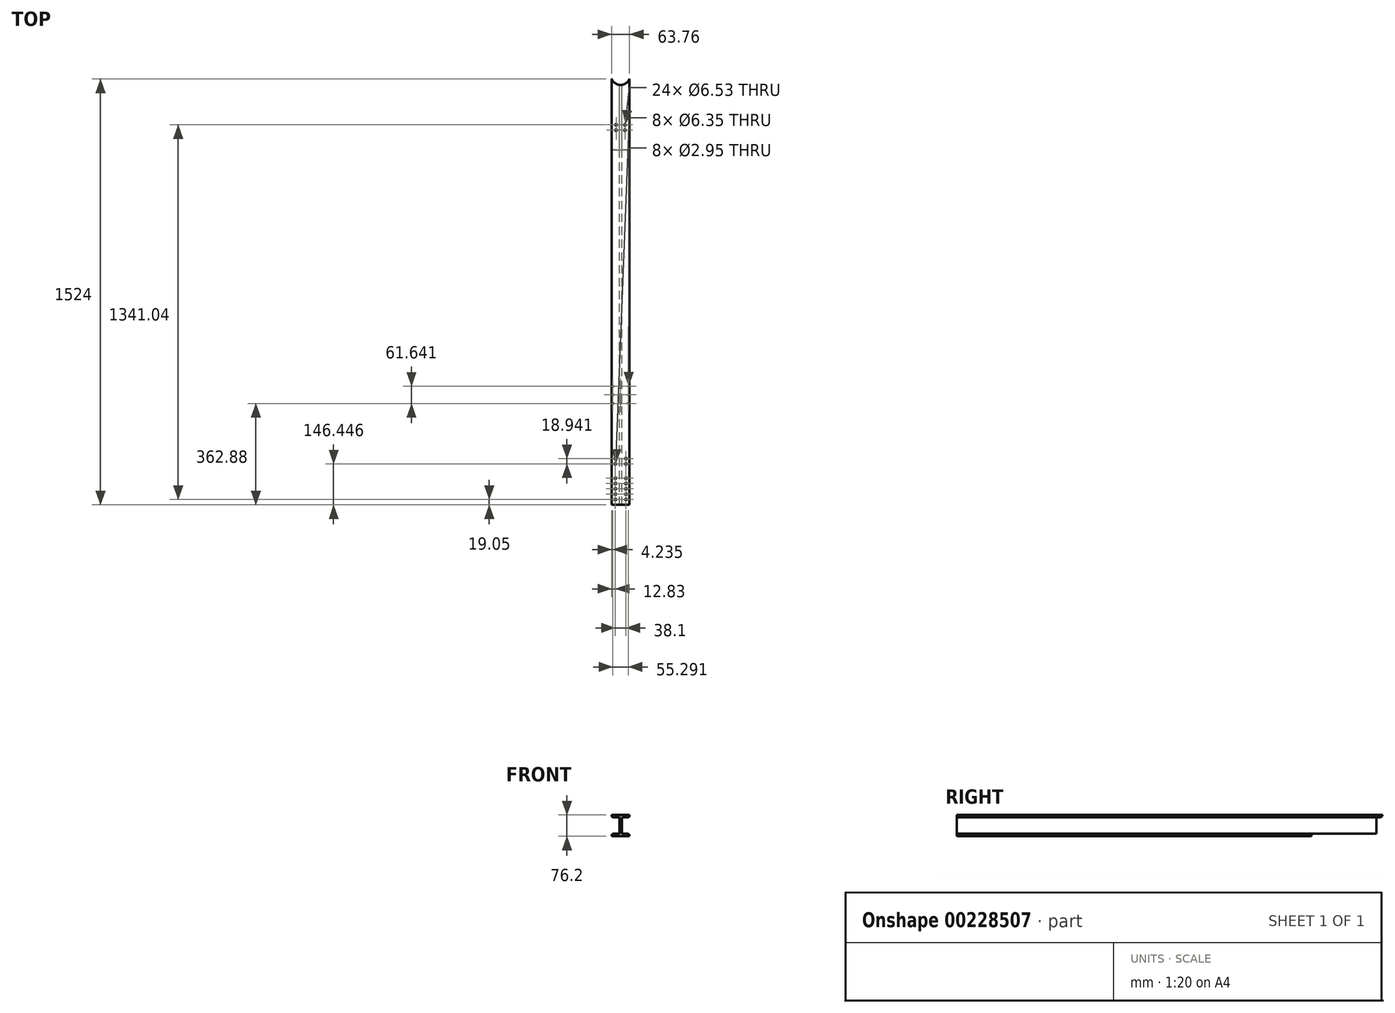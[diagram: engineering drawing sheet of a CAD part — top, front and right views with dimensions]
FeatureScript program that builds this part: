
annotation { "Feature Type Name" : "Feature", "Feature Type Description" : "" }
export const myFeature = defineFeature(function(context is Context, id is Id, definition is map)
    precondition{}
    {
        {
            var Q0;
            Q0=qCreatedBy(makeId("Front.planeOp"),FACE);
            var sketch = newSketch(context, id + "F0", { "sketchPlane" : qUnion([Q0])});
            skLineSegment(sketch, "E0", {"start": v(0, 0) * mm, "end": v(0, 38.1) * mm});
            skLineSegment(sketch, "E1", {"start": v(0, 38.1) * mm, "end": v(31.88, 38.1) * mm});
            skLineSegment(sketch, "E2", {"start": v(31.88, 38.1) * mm, "end": v(31.88, 35.56) * mm});
            skLineSegment(sketch, "E3", {"start": v(0, 0) * mm, "end": v(4.45, 0) * mm});
            skLineSegment(sketch, "E4", {"start": v(4.45, 0) * mm, "end": v(4.45, 29.2) * mm});
            skLineSegment(sketch, "E5", {"start": v(4.44, 29.2) * mm, "end": v(25.53, 29.2) * mm});
            skPoint(sketch, "E6.visualSharp", {"position": v(31.88, 29.2) * mm});
            skArc(sketch, "E6.filletArc", {"start": v(25.53, 29.2) * mm, "mid": v(30.02, 31.07) * mm, "end": v(31.88, 35.56) * mm});
            skLineSegment(sketch, "E7.MirrorCS", {"start": v(4.45, 0) * mm, "end": v(4.45, -29.2) * mm});
            skLineSegment(sketch, "E8.MirrorCS", {"start": v(4.44, -29.2) * mm, "end": v(25.53, -29.2) * mm});
            skLineSegment(sketch, "E9.MirrorCS", {"start": v(0, 0) * mm, "end": v(0, -38.1) * mm});
            skLineSegment(sketch, "E10.MirrorCS", {"start": v(0, -38.1) * mm, "end": v(31.88, -38.1) * mm});
            skArc(sketch, "E11.MirrorCS", {"start": v(25.53, -29.2) * mm, "mid": v(30.02, -31.07) * mm, "end": v(31.88, -35.56) * mm});
            skLineSegment(sketch, "E12.MirrorCS", {"start": v(31.88, -38.1) * mm, "end": v(31.88, -35.56) * mm});
            skLineSegment(sketch, "E13.MirrorCS", {"start": v(0, 38.1) * mm, "end": v(-31.88, 38.1) * mm});
            skLineSegment(sketch, "E14.MirrorCS", {"start": v(-31.88, 38.1) * mm, "end": v(-31.88, 35.56) * mm});
            skArc(sketch, "E15.MirrorCS", {"start": v(-25.53, 29.2) * mm, "mid": v(-30.02, 31.07) * mm, "end": v(-31.88, 35.56) * mm});
            skLineSegment(sketch, "E16.MirrorCS", {"start": v(-4.44, 29.2) * mm, "end": v(-25.53, 29.2) * mm});
            skLineSegment(sketch, "E17.MirrorCS", {"start": v(-4.45, 0) * mm, "end": v(-4.45, -29.2) * mm});
            skLineSegment(sketch, "E18.MirrorCS", {"start": v(-4.44, -29.2) * mm, "end": v(-25.53, -29.2) * mm});
            skArc(sketch, "E19.MirrorCS", {"start": v(-25.53, -29.2) * mm, "mid": v(-30.02, -31.07) * mm, "end": v(-31.88, -35.56) * mm});
            skLineSegment(sketch, "E20.MirrorCS", {"start": v(-4.45, 0) * mm, "end": v(-4.45, 29.2) * mm});
            skLineSegment(sketch, "E21.MirrorCS", {"start": v(-31.88, -38.1) * mm, "end": v(-31.88, -35.56) * mm});
            skLineSegment(sketch, "E22.MirrorCS", {"start": v(0, -38.1) * mm, "end": v(-31.88, -38.1) * mm});
            skSolve(sketch);
        }
        {
            var Q0;
            Q0 = qSketchRegion(id + "F0", true);
            extrude(context, id + "F1", {"entities" : qUnion([Q0]), "depth" : 1524 * mm});
        }
        {
            var Q0;
            Q0=makeQuery(id+"F1.opExtrude","SWEPT_FACE",FACE,{"disambiguationData":[OSD([sQuery(id+"F0.wireOp",EDGE,"E1"),sQuery(id+"F0.wireOp",EDGE,"E13.MirrorCS")])]});
            var sketch = newSketch(context, id + "F2", { "sketchPlane" : qUnion([Q0])});
            skLineSegment(sketch, "E23", {"start": v(0, -35.6) * mm, "end": v(0, 13.64) * mm});
            skCircle(sketch, "E24", {"center": v(0, 13.64) * mm, "radius": 34.67 * mm});
            skLineSegment(sketch, "E25", {"start": v(0, 0) * mm, "end": v(-31.88, 0) * mm});
            skSolve(sketch);
        }
        {
            var Q0;
            Q0 = qSketchRegion(id + "F2", true);
            extrude(context, id + "F3", {"entities" : qUnion([Q0]), "operationType" : NewBodyOperationType.REMOVE, "oppositeDirection" : true, "depth" : 101.6 * mm});
        }
        {
            var Q0;
            Q0=makeQuery(id+"F1.opExtrude","SWEPT_FACE",FACE,{"disambiguationData":[OSD([sQuery(id+"F0.wireOp",EDGE,"E1"),sQuery(id+"F0.wireOp",EDGE,"E13.MirrorCS")])]});
            var sketch = newSketch(context, id + "F4", { "sketchPlane" : qUnion([Q0])});
            skLineSegment(sketch, "E26", {"start": v(0, -21.04) * mm, "end": v(0, -173.44) * mm});
            skPoint(sketch, "E26.endSnap0", {"position": v(0, -21.04) * mm});
            skLineSegment(sketch, "E27.bottom", {"start": v(15.88, -182.96) * mm, "end": v(-15.87, -182.96) * mm});
            skLineSegment(sketch, "E27.top", {"start": v(15.88, -163.91) * mm, "end": v(-15.87, -163.91) * mm});
            skLineSegment(sketch, "E27.left", {"start": v(15.88, -182.96) * mm, "end": v(15.88, -163.91) * mm});
            skLineSegment(sketch, "E27.right", {"start": v(-15.87, -182.96) * mm, "end": v(-15.87, -163.91) * mm});
            skPoint(sketch, "E27.middle", {"position": v(0, -173.44) * mm});
            skSolve(sketch);
        }
        {
            var Q0;
            Q0=sQuery(id+"F4.wireOp",VERTEX,"E27.bottom.end");
            var Q1;
            Q1=sQuery(id+"F4.wireOp",VERTEX,"E27.top.start");
            var Q2;
            Q2=sQuery(id+"F4.wireOp",VERTEX,"E27.left.start");
            var Q3;
            Q3=sQuery(id+"F4.wireOp",VERTEX,"E27.top.end");
            var Q4;
            Q4=makeQuery(id+"F1.opExtrude","SWEPT_BODY",BODY,{"disambiguationData":[OSD([sQuery(id+"F0.wireOp",EDGE,"E1"),sQuery(id+"F0.wireOp",EDGE,"E2"),sQuery(id+"F0.wireOp",EDGE,"E4"),sQuery(id+"F0.wireOp",EDGE,"E5"),sQuery(id+"F0.wireOp",EDGE,"E6.filletArc"),sQuery(id+"F0.wireOp",EDGE,"E7.MirrorCS"),sQuery(id+"F0.wireOp",EDGE,"E8.MirrorCS"),sQuery(id+"F0.wireOp",EDGE,"E10.MirrorCS"),sQuery(id+"F0.wireOp",EDGE,"E11.MirrorCS"),sQuery(id+"F0.wireOp",EDGE,"E12.MirrorCS"),sQuery(id+"F0.wireOp",EDGE,"E13.MirrorCS"),sQuery(id+"F0.wireOp",EDGE,"E14.MirrorCS"),sQuery(id+"F0.wireOp",EDGE,"E15.MirrorCS"),sQuery(id+"F0.wireOp",EDGE,"E16.MirrorCS"),sQuery(id+"F0.wireOp",EDGE,"E17.MirrorCS"),sQuery(id+"F0.wireOp",EDGE,"E18.MirrorCS"),sQuery(id+"F0.wireOp",EDGE,"E19.MirrorCS"),sQuery(id+"F0.wireOp",EDGE,"E20.MirrorCS"),sQuery(id+"F0.wireOp",EDGE,"E21.MirrorCS"),sQuery(id+"F0.wireOp",EDGE,"E22.MirrorCS")])]});
            hole(context, id + "F5", {"style" : HoleStyle.SIMPLE, "endStyle" : HoleEndStyle.BLIND, "standardTappedOrClearance" : lookupTablePath({ "standard" : "ANSI", "fit" : "Close", "size" : "1/4", "type" : "Clearance" }), "standardBlindInLast" : lookupTablePath({ "fit" : "Close", "standard" : "ANSI", "size" : "1/4", "type" : "Clearance" }), "holeDiameter" : 6.53 * mm, "holeDepth" : 12.7 * mm, "locations" : qUnion([Q0, Q1, Q2, Q3]), "scope" : qUnion([Q4])});
        }
        {
            var Q0;
            Q0=qCreatedBy(makeId("Front.planeOp"),FACE);
            var sketch = newSketch(context, id + "F6", { "sketchPlane" : qUnion([Q0])});
            skLineSegment(sketch, "E28", {"start": v(4.45, -29.21) * mm, "end": v(40, -29.21) * mm});
            skLineSegment(sketch, "E29", {"start": v(40, -29.21) * mm, "end": v(40, -38.1) * mm});
            skLineSegment(sketch, "E30.MirrorCS", {"start": v(-4.45, -29.21) * mm, "end": v(-40, -29.21) * mm});
            skLineSegment(sketch, "E31.MirrorCS", {"start": v(-40, -29.21) * mm, "end": v(-40, -38.1) * mm});
            skLineSegment(sketch, "E32", {"start": v(40, -38.1) * mm, "end": v(-40, -38.1) * mm});
            skLineSegment(sketch, "E33", {"start": v(-4.45, -29.21) * mm, "end": v(4.45, -29.21) * mm});
            skSolve(sketch);
        }
        {
            var Q0;
            Q0 = qSketchRegion(id + "F6", true);
            extrude(context, id + "F7", {"entities" : qUnion([Q0]), "operationType" : NewBodyOperationType.REMOVE, "depth" : 254 * mm});
        }
        {
            var Q0;
            Q0=makeQuery(id+"F1.opExtrude","SWEPT_FACE",FACE,{"disambiguationData":[OSD([sQuery(id+"F0.wireOp",EDGE,"E1"),sQuery(id+"F0.wireOp",EDGE,"E13.MirrorCS")])]});
            var sketch = newSketch(context, id + "F8", { "sketchPlane" : qUnion([Q0])});
            skLineSegment(sketch, "E34", {"start": v(0, -1524) * mm, "end": v(0, -1504.95) * mm});
            skLineSegment(sketch, "E35", {"start": v(0, -1504.95) * mm, "end": v(19.05, -1504.95) * mm});
            skLineSegment(sketch, "E36", {"start": v(19.05, -1504.95) * mm, "end": v(19.05, -1485.9) * mm});
            skLineSegment(sketch, "E37", {"start": v(19.05, -1485.9) * mm, "end": v(19.05, -1466.85) * mm});
            skLineSegment(sketch, "E38", {"start": v(19.05, -1466.85) * mm, "end": v(19.05, -1447.8) * mm});
            skLineSegment(sketch, "E39", {"start": v(19.05, -1447.8) * mm, "end": v(19.05, -1428.75) * mm});
            skLineSegment(sketch, "E40.MirrorCS", {"start": v(0, -1504.95) * mm, "end": v(-19.05, -1504.95) * mm});
            skLineSegment(sketch, "E41.MirrorCS", {"start": v(-19.05, -1504.95) * mm, "end": v(-19.05, -1485.9) * mm});
            skLineSegment(sketch, "E42.MirrorCS", {"start": v(-19.05, -1485.9) * mm, "end": v(-19.05, -1466.85) * mm});
            skLineSegment(sketch, "E43.MirrorCS", {"start": v(-19.05, -1466.85) * mm, "end": v(-19.05, -1447.8) * mm});
            skLineSegment(sketch, "E44.MirrorCS", {"start": v(-19.05, -1447.8) * mm, "end": v(-19.05, -1428.75) * mm});
            skPoint(sketch, "E45", {"position": v(-19.05, -1428.75) * mm});
            skPoint(sketch, "E46", {"position": v(-19.05, -1377.55) * mm});
            skPoint(sketch, "E47", {"position": v(19.05, -1428.75) * mm});
            skPoint(sketch, "E48", {"position": v(19.05, -1377.55) * mm});
            skPoint(sketch, "E49", {"position": v(-19.05, -1358.61) * mm});
            skPoint(sketch, "E50", {"position": v(19.05, -1358.61) * mm});
            skSolve(sketch);
        }
        {
            var Q0;
            Q0=sQuery(id+"F8.wireOp",VERTEX,"E44.MirrorCS.end");
            var Q1;
            Q1=sQuery(id+"F8.wireOp",VERTEX,"E43.MirrorCS.end");
            var Q2;
            Q2=sQuery(id+"F8.wireOp",VERTEX,"E42.MirrorCS.end");
            var Q3;
            Q3=sQuery(id+"F8.wireOp",VERTEX,"E41.MirrorCS.end");
            var Q4;
            Q4=sQuery(id+"F8.wireOp",VERTEX,"E41.MirrorCS.start");
            var Q5;
            Q5=sQuery(id+"F8.wireOp",VERTEX,"E36.start");
            var Q6;
            Q6=sQuery(id+"F8.wireOp",VERTEX,"E37.start");
            var Q7;
            Q7=sQuery(id+"F8.wireOp",VERTEX,"E38.start");
            var Q8;
            Q8=sQuery(id+"F8.wireOp",VERTEX,"E38.end");
            var Q9;
            Q9=sQuery(id+"F8.wireOp",VERTEX,"E39.end");
            var Q10;
            Q10=makeQuery(id+"F1.opExtrude","SWEPT_BODY",BODY,{"disambiguationData":[OSD([sQuery(id+"F0.wireOp",EDGE,"E1"),sQuery(id+"F0.wireOp",EDGE,"E2"),sQuery(id+"F0.wireOp",EDGE,"E4"),sQuery(id+"F0.wireOp",EDGE,"E5"),sQuery(id+"F0.wireOp",EDGE,"E6.filletArc"),sQuery(id+"F0.wireOp",EDGE,"E7.MirrorCS"),sQuery(id+"F0.wireOp",EDGE,"E8.MirrorCS"),sQuery(id+"F0.wireOp",EDGE,"E10.MirrorCS"),sQuery(id+"F0.wireOp",EDGE,"E11.MirrorCS"),sQuery(id+"F0.wireOp",EDGE,"E12.MirrorCS"),sQuery(id+"F0.wireOp",EDGE,"E13.MirrorCS"),sQuery(id+"F0.wireOp",EDGE,"E14.MirrorCS"),sQuery(id+"F0.wireOp",EDGE,"E15.MirrorCS"),sQuery(id+"F0.wireOp",EDGE,"E16.MirrorCS"),sQuery(id+"F0.wireOp",EDGE,"E17.MirrorCS"),sQuery(id+"F0.wireOp",EDGE,"E18.MirrorCS"),sQuery(id+"F0.wireOp",EDGE,"E19.MirrorCS"),sQuery(id+"F0.wireOp",EDGE,"E20.MirrorCS"),sQuery(id+"F0.wireOp",EDGE,"E21.MirrorCS"),sQuery(id+"F0.wireOp",EDGE,"E22.MirrorCS")])]});
            hole(context, id + "F9", {"style" : HoleStyle.SIMPLE, "endStyle" : HoleEndStyle.BLIND, "standardTappedOrClearance" : lookupTablePath({ "standard" : "ANSI", "fit" : "Close", "size" : "1/4", "type" : "Clearance" }), "standardBlindInLast" : lookupTablePath({ "fit" : "Close", "standard" : "ANSI", "size" : "1/4", "type" : "Clearance" }), "holeDiameter" : 6.53 * mm, "holeDepth" : 101.6 * mm, "locations" : qUnion([Q0, Q1, Q2, Q3, Q4, Q5, Q6, Q7, Q8, Q9]), "scope" : qUnion([Q10])});
        }
        {
            var Q0;
            Q0=sQuery(id+"F8.wireOp",VERTEX,"E48");
            var Q1;
            Q1=sQuery(id+"F8.wireOp",VERTEX,"E50");
            var Q2;
            Q2=sQuery(id+"F8.wireOp",VERTEX,"E49");
            var Q3;
            Q3=sQuery(id+"F8.wireOp",VERTEX,"E46");
            var Q4;
            Q4=makeQuery(id+"F1.opExtrude","SWEPT_BODY",BODY,{"disambiguationData":[OSD([sQuery(id+"F0.wireOp",EDGE,"E1"),sQuery(id+"F0.wireOp",EDGE,"E2"),sQuery(id+"F0.wireOp",EDGE,"E4"),sQuery(id+"F0.wireOp",EDGE,"E5"),sQuery(id+"F0.wireOp",EDGE,"E6.filletArc"),sQuery(id+"F0.wireOp",EDGE,"E7.MirrorCS"),sQuery(id+"F0.wireOp",EDGE,"E8.MirrorCS"),sQuery(id+"F0.wireOp",EDGE,"E10.MirrorCS"),sQuery(id+"F0.wireOp",EDGE,"E11.MirrorCS"),sQuery(id+"F0.wireOp",EDGE,"E12.MirrorCS"),sQuery(id+"F0.wireOp",EDGE,"E13.MirrorCS"),sQuery(id+"F0.wireOp",EDGE,"E14.MirrorCS"),sQuery(id+"F0.wireOp",EDGE,"E15.MirrorCS"),sQuery(id+"F0.wireOp",EDGE,"E16.MirrorCS"),sQuery(id+"F0.wireOp",EDGE,"E17.MirrorCS"),sQuery(id+"F0.wireOp",EDGE,"E18.MirrorCS"),sQuery(id+"F0.wireOp",EDGE,"E19.MirrorCS"),sQuery(id+"F0.wireOp",EDGE,"E20.MirrorCS"),sQuery(id+"F0.wireOp",EDGE,"E21.MirrorCS"),sQuery(id+"F0.wireOp",EDGE,"E22.MirrorCS")])]});
            hole(context, id + "F10", {"style" : HoleStyle.SIMPLE, "endStyle" : HoleEndStyle.THROUGH, "holeDiameter" : 6.35 * mm, "locations" : qUnion([Q0, Q1, Q2, Q3]), "scope" : qUnion([Q4]), "isTappedThrough" : true});
        }
        {
            var Q0;
            Q0=makeQuery(id+"F1.opExtrude","SWEPT_FACE",FACE,{"disambiguationData":[OSD([sQuery(id+"F0.wireOp",EDGE,"E1"),sQuery(id+"F0.wireOp",EDGE,"E13.MirrorCS")])]});
            var sketch = newSketch(context, id + "F11", { "sketchPlane" : qUnion([Q0])});
            skLineSegment(sketch, "E51", {"start": v(0, -1524) * mm, "end": v(0, -1130.3) * mm});
            skLineSegment(sketch, "E52.bottom", {"start": v(-27.65, -1161.12) * mm, "end": v(27.65, -1161.12) * mm});
            skLineSegment(sketch, "E52.top", {"start": v(-27.65, -1099.48) * mm, "end": v(27.65, -1099.48) * mm});
            skLineSegment(sketch, "E52.left", {"start": v(-27.65, -1161.12) * mm, "end": v(-27.65, -1099.48) * mm});
            skLineSegment(sketch, "E52.right", {"start": v(27.65, -1161.12) * mm, "end": v(27.65, -1099.48) * mm});
            skPoint(sketch, "E52.middle", {"position": v(0, -1130.3) * mm});
            skLineSegment(sketch, "E53", {"start": v(27.65, -1130.3) * mm, "end": v(-27.65, -1130.3) * mm});
            skLineSegment(sketch, "E54", {"start": v(0, -1099.48) * mm, "end": v(0, -1161.12) * mm});
            skSolve(sketch);
        }
        {
            var Q0;
            Q0=sQuery(id+"F11.wireOp",VERTEX,"E52.top.end");
            var Q1;
            Q1=sQuery(id+"F11.wireOp",VERTEX,"E53.start");
            var Q2;
            Q2=sQuery(id+"F11.wireOp",VERTEX,"E54.start");
            var Q3;
            Q3=sQuery(id+"F11.wireOp",VERTEX,"E52.top.start");
            var Q4;
            Q4=sQuery(id+"F11.wireOp",VERTEX,"E53.end");
            var Q5;
            Q5=sQuery(id+"F11.wireOp",VERTEX,"E52.left.start");
            var Q6;
            Q6=sQuery(id+"F11.wireOp",VERTEX,"E54.end");
            var Q7;
            Q7=sQuery(id+"F11.wireOp",VERTEX,"E52.bottom.end");
            var Q8;
            Q8=makeQuery(id+"F1.opExtrude","SWEPT_BODY",BODY,{"disambiguationData":[OSD([sQuery(id+"F0.wireOp",EDGE,"E1"),sQuery(id+"F0.wireOp",EDGE,"E2"),sQuery(id+"F0.wireOp",EDGE,"E4"),sQuery(id+"F0.wireOp",EDGE,"E5"),sQuery(id+"F0.wireOp",EDGE,"E6.filletArc"),sQuery(id+"F0.wireOp",EDGE,"E7.MirrorCS"),sQuery(id+"F0.wireOp",EDGE,"E8.MirrorCS"),sQuery(id+"F0.wireOp",EDGE,"E10.MirrorCS"),sQuery(id+"F0.wireOp",EDGE,"E11.MirrorCS"),sQuery(id+"F0.wireOp",EDGE,"E12.MirrorCS"),sQuery(id+"F0.wireOp",EDGE,"E13.MirrorCS"),sQuery(id+"F0.wireOp",EDGE,"E14.MirrorCS"),sQuery(id+"F0.wireOp",EDGE,"E15.MirrorCS"),sQuery(id+"F0.wireOp",EDGE,"E16.MirrorCS"),sQuery(id+"F0.wireOp",EDGE,"E17.MirrorCS"),sQuery(id+"F0.wireOp",EDGE,"E18.MirrorCS"),sQuery(id+"F0.wireOp",EDGE,"E19.MirrorCS"),sQuery(id+"F0.wireOp",EDGE,"E20.MirrorCS"),sQuery(id+"F0.wireOp",EDGE,"E21.MirrorCS"),sQuery(id+"F0.wireOp",EDGE,"E22.MirrorCS")])]});
            hole(context, id + "F12", {"style" : HoleStyle.SIMPLE, "endStyle" : HoleEndStyle.BLIND, "standardTappedOrClearance" : lookupTablePath({ "standard" : "ANSI", "fit" : "Close", "size" : "#4", "type" : "Clearance" }), "standardBlindInLast" : lookupTablePath({ "fit" : "Close", "standard" : "ANSI", "size" : "#4", "type" : "Clearance" }), "holeDiameter" : 2.95 * mm, "holeDepth" : 5.08 * mm, "tappedDepth" : 10.8 * mm, "tapClearance" : 3, "locations" : qUnion([Q0, Q1, Q2, Q3, Q4, Q5, Q6, Q7]), "scope" : qUnion([Q8])});
        }
    });
